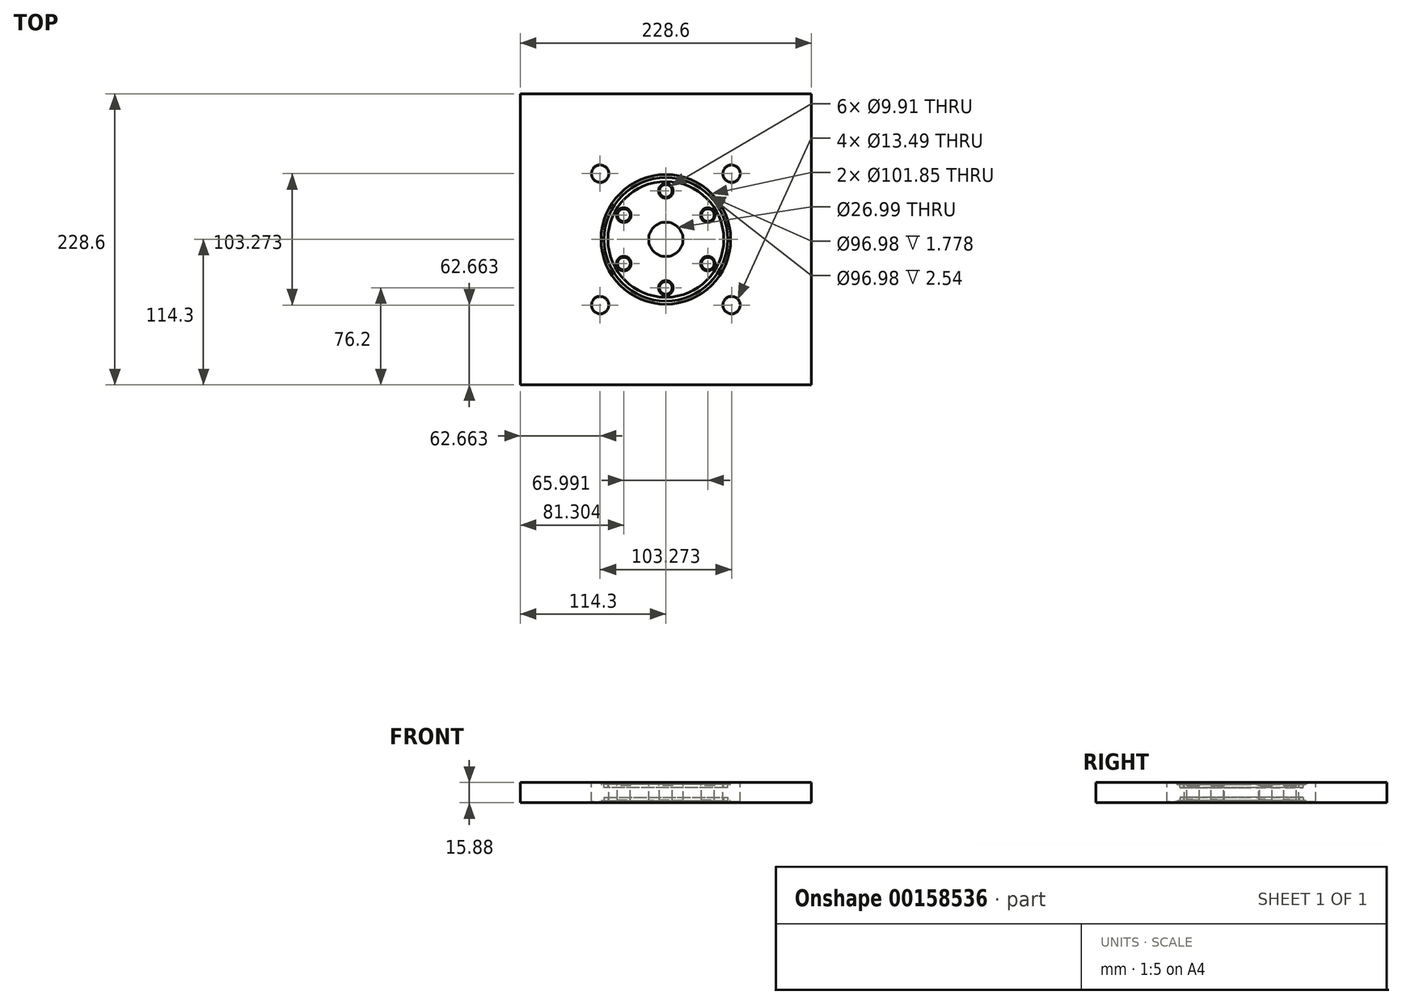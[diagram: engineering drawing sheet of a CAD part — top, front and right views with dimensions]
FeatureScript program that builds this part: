
annotation { "Feature Type Name" : "Feature", "Feature Type Description" : "" }
export const myFeature = defineFeature(function(context is Context, id is Id, definition is map)
    precondition{}
    {
        {
            var Q0;
            Q0=qCreatedBy(makeId("Top.planeOp"),FACE);
            var sketch = newSketch(context, id + "F0", { "sketchPlane" : qUnion([Q0])});
            skCircle(sketch, "E0", {"center": v(0, 0) * mm, "radius": 95.25 * mm});
            skLineSegment(sketch, "E1", {"start": v(-114.3, 114.3) * mm, "end": v(-98.43, 114.3) * mm});
            skLineSegment(sketch, "E2", {"start": v(-114.3, 114.3) * mm, "end": v(-114.3, 74.18) * mm});
            skLineSegment(sketch, "E3", {"start": v(-114.3, 74.18) * mm, "end": v(-89.8, 31.75) * mm});
            skLineSegment(sketch, "E4", {"start": v(-98.43, 114.3) * mm, "end": v(-58.95, 74.82) * mm});
            skLineSegment(sketch, "E5", {"start": v(0, 150.47) * mm, "end": v(0, -152.8) * mm, "construction": true});
            skLineSegment(sketch, "E6.MirrorCS", {"start": v(114.3, 74.18) * mm, "end": v(89.8, 31.75) * mm});
            skLineSegment(sketch, "E7.MirrorCS", {"start": v(114.3, 114.3) * mm, "end": v(114.3, 74.18) * mm});
            skLineSegment(sketch, "E8.MirrorCS", {"start": v(98.42, 114.3) * mm, "end": v(58.95, 74.82) * mm});
            skLineSegment(sketch, "E9.MirrorCS", {"start": v(114.3, 114.3) * mm, "end": v(98.43, 114.3) * mm});
            skLineSegment(sketch, "E10", {"start": v(-127.05, 0) * mm, "end": v(124.38, 0) * mm, "construction": true});
            skLineSegment(sketch, "E11.MirrorCS", {"start": v(-114.3, -114.3) * mm, "end": v(-98.43, -114.3) * mm});
            skLineSegment(sketch, "E12.MirrorCS", {"start": v(114.3, -114.3) * mm, "end": v(98.43, -114.3) * mm});
            skLineSegment(sketch, "E13.MirrorCS", {"start": v(-114.3, -74.18) * mm, "end": v(-89.8, -31.75) * mm});
            skLineSegment(sketch, "E14.MirrorCS", {"start": v(-98.42, -114.3) * mm, "end": v(-58.95, -74.82) * mm});
            skLineSegment(sketch, "E15.MirrorCS", {"start": v(-114.3, -114.3) * mm, "end": v(-114.3, -74.18) * mm});
            skLineSegment(sketch, "E16.MirrorCS", {"start": v(98.43, -114.3) * mm, "end": v(58.95, -74.82) * mm});
            skLineSegment(sketch, "E17.MirrorCS", {"start": v(114.3, -114.3) * mm, "end": v(114.3, -74.18) * mm});
            skLineSegment(sketch, "E18.MirrorCS", {"start": v(114.3, -74.18) * mm, "end": v(89.8, -31.75) * mm});
            skLineSegment(sketch, "E19", {"start": v(-98.43, 114.3) * mm, "end": v(98.43, 114.3) * mm});
            skLineSegment(sketch, "E20", {"start": v(114.3, 74.18) * mm, "end": v(114.3, -74.18) * mm});
            skLineSegment(sketch, "E21", {"start": v(98.43, -114.3) * mm, "end": v(-98.43, -114.3) * mm});
            skLineSegment(sketch, "E22", {"start": v(-114.3, -74.18) * mm, "end": v(-114.3, 74.18) * mm});
            skSolve(sketch);
        }
        {
            var Q0;
            {var subQ1=sQuery(id+"F0.wireOp",EDGE,"E6.MirrorCS");Q0=makeQuery(id+"F0.imprint","IMPRINT",FACE,{"disambiguationData":[TD([[makeQuery(id+"F0.imprint","IMPRINT",EDGE,{"derivedFrom":subQ1}),-1.0]])]});}
            var Q1;
            Q1=makeQuery(id+"F0.imprint","IMPRINT",FACE,{"disambiguationData":[TD([[makeQuery(id+"F0.imprint","IMPRINT",EDGE,{"derivedFrom":sQuery(id+"F0.wireOp",EDGE,"E1")}),-1.0]])]});
            var Q2;
            Q2=makeQuery(id+"F0.imprint","IMPRINT",FACE,{"disambiguationData":[TD([[makeQuery(id+"F0.imprint","IMPRINT",EDGE,{"derivedFrom":sQuery(id+"F0.wireOp",EDGE,"E11.MirrorCS")}),1.0]])]});
            var Q3;
            Q3=makeQuery(id+"F0.imprint","IMPRINT",FACE,{"disambiguationData":[TD([[makeQuery(id+"F0.imprint","IMPRINT",EDGE,{"derivedFrom":sQuery(id+"F0.wireOp",EDGE,"E12.MirrorCS")}),-1.0]])]});
            var Q4;
            {var subQ0=sQuery(id+"F0.wireOp",EDGE,"E0");var subQ5=makeQuery(id+"F0.imprint","INTERSECT",VERTEX,{"derivedFrom":[subQ0,sQuery(id+"F0.wireOp",EDGE,"E6.MirrorCS")]});Q4=makeQuery(id+"F0.imprint","IMPRINT",FACE,{"disambiguationData":[TD([[makeQuery(id+"F0.imprint","IMPRINT",EDGE,{"disambiguationData":[TD([[subQ5,-1.0]])],"derivedFrom":subQ0}),1.0]])]});}
            var Q5;
            Q5 = qSketchRegion(id + "F2", true);
            var Q6;
            {var subQ0=sQuery(id+"F0.wireOp",EDGE,"E4");Q6=makeQuery(id+"F0.imprint","IMPRINT",FACE,{"disambiguationData":[TD([[makeQuery(id+"F0.imprint","IMPRINT",EDGE,{"derivedFrom":subQ0}),1.0]])]});}
            var Q7;
            {var subQ0=sQuery(id+"F0.wireOp",EDGE,"E6.MirrorCS");Q7=makeQuery(id+"F0.imprint","IMPRINT",FACE,{"disambiguationData":[TD([[makeQuery(id+"F0.imprint","IMPRINT",EDGE,{"derivedFrom":subQ0}),1.0]])]});}
            var Q8;
            {var subQ0=sQuery(id+"F0.wireOp",EDGE,"E14.MirrorCS");Q8=makeQuery(id+"F0.imprint","IMPRINT",FACE,{"disambiguationData":[TD([[makeQuery(id+"F0.imprint","IMPRINT",EDGE,{"derivedFrom":subQ0}),-1.0]])]});}
            var Q9;
            {var subQ0=sQuery(id+"F0.wireOp",EDGE,"E3");Q9=makeQuery(id+"F0.imprint","IMPRINT",FACE,{"disambiguationData":[TD([[makeQuery(id+"F0.imprint","IMPRINT",EDGE,{"derivedFrom":subQ0}),-1.0]])]});}
            extrude(context, id + "F1", {"entities" : qUnion([Q0, Q1, Q2, Q3, Q4, Q5, Q6, Q7, Q8, Q9]), "depth" : 15.88 * mm});
        }
        {
            var Q0;
            Q0=makeQuery(id+"F1.opExtrude","CAP_FACE",FACE,{"disambiguationData":[OSD([sQuery(id+"F0.wireOp",EDGE,"E0"),sQuery(id+"F0.wireOp",EDGE,"E1"),sQuery(id+"F0.wireOp",EDGE,"E2"),sQuery(id+"F0.wireOp",EDGE,"E3"),sQuery(id+"F0.wireOp",EDGE,"E4"),sQuery(id+"F0.wireOp",EDGE,"E6.MirrorCS"),sQuery(id+"F0.wireOp",EDGE,"E7.MirrorCS"),sQuery(id+"F0.wireOp",EDGE,"E8.MirrorCS"),sQuery(id+"F0.wireOp",EDGE,"E9.MirrorCS"),sQuery(id+"F0.wireOp",EDGE,"E11.MirrorCS"),sQuery(id+"F0.wireOp",EDGE,"E12.MirrorCS"),sQuery(id+"F0.wireOp",EDGE,"E13.MirrorCS"),sQuery(id+"F0.wireOp",EDGE,"E14.MirrorCS"),sQuery(id+"F0.wireOp",EDGE,"E15.MirrorCS"),sQuery(id+"F0.wireOp",EDGE,"E16.MirrorCS"),sQuery(id+"F0.wireOp",EDGE,"E17.MirrorCS"),sQuery(id+"F0.wireOp",EDGE,"E18.MirrorCS")])],"isStart":false});
            var sketch = newSketch(context, id + "F2", { "sketchPlane" : qUnion([Q0])});
            skLineSegment(sketch, "E23", {"start": v(0, 0) * mm, "end": v(74.38, 0) * mm, "construction": true});
            skLineSegment(sketch, "E24", {"start": v(0, 0) * mm, "end": v(51.64, 51.64) * mm, "construction": true});
            skCircle(sketch, "E25", {"center": v(51.64, 51.64) * mm, "radius": 6.75 * mm});
            skCircle(sketch, "E26.1.0", {"center": v(-51.64, 51.64) * mm, "radius": 6.75 * mm});
            skCircle(sketch, "E26.2.0", {"center": v(-51.64, -51.64) * mm, "radius": 6.75 * mm});
            skCircle(sketch, "E26.3.0", {"center": v(51.64, -51.64) * mm, "radius": 6.75 * mm});
            skPoint(sketch, "E26.center", {"position": v(0, 0) * mm});
            skSolve(sketch);
        }
        {
            var Q0;
            Q0 = qSketchRegion(id + "F2", true);
            extrude(context, id + "F3", {"entities" : qUnion([Q0]), "operationType" : NewBodyOperationType.REMOVE, "oppositeDirection" : true, "depth" : 25.4 * mm});
        }
        {
            var Q0;
            Q0=makeQuery(id+"F1.opExtrude","CAP_FACE",FACE,{"disambiguationData":[OSD([sQuery(id+"F0.wireOp",EDGE,"E1"),sQuery(id+"F0.wireOp",EDGE,"E2"),sQuery(id+"F0.wireOp",EDGE,"E7.MirrorCS"),sQuery(id+"F0.wireOp",EDGE,"E9.MirrorCS"),sQuery(id+"F0.wireOp",EDGE,"E11.MirrorCS"),sQuery(id+"F0.wireOp",EDGE,"E12.MirrorCS"),sQuery(id+"F0.wireOp",EDGE,"E15.MirrorCS"),sQuery(id+"F0.wireOp",EDGE,"E17.MirrorCS"),sQuery(id+"F0.wireOp",EDGE,"E19"),sQuery(id+"F0.wireOp",EDGE,"E20"),sQuery(id+"F0.wireOp",EDGE,"E21"),sQuery(id+"F0.wireOp",EDGE,"E22")])],"isStart":false});
            var sketch = newSketch(context, id + "F4", { "sketchPlane" : qUnion([Q0])});
            skCircle(sketch, "E27", {"center": v(0, 0) * mm, "radius": 50.93 * mm});
            skCircle(sketch, "E28", {"center": v(0, 0) * mm, "radius": 13.5 * mm});
            skSolve(sketch);
        }
        {
            var Q0;
            Q0=makeQuery(id+"F4.imprint","IMPRINT",FACE,{"disambiguationData":[TD([[makeQuery(id+"F4.imprint","IMPRINT",EDGE,{"derivedFrom":sQuery(id+"F4.wireOp",EDGE,"E27")}),1.0]])]});
            extrude(context, id + "F5", {"entities" : qUnion([Q0]), "operationType" : NewBodyOperationType.REMOVE, "oppositeDirection" : true, "depth" : 1.59 * mm});
        }
        {
            var Q0;
            Q0=makeQuery(id+"F4.imprint","IMPRINT",FACE,{"disambiguationData":[TD([[makeQuery(id+"F4.imprint","IMPRINT",EDGE,{"derivedFrom":sQuery(id+"F4.wireOp",EDGE,"E28")}),1.0]])]});
            extrude(context, id + "F6", {"entities" : qUnion([Q0]), "operationType" : NewBodyOperationType.REMOVE, "oppositeDirection" : true, "depth" : 25.4 * mm});
        }
        {
            var Q0;
            Q0=makeQuery(id+"F1.opExtrude","CAP_FACE",FACE,{"disambiguationData":[OSD([sQuery(id+"F0.wireOp",EDGE,"E1"),sQuery(id+"F0.wireOp",EDGE,"E2"),sQuery(id+"F0.wireOp",EDGE,"E7.MirrorCS"),sQuery(id+"F0.wireOp",EDGE,"E9.MirrorCS"),sQuery(id+"F0.wireOp",EDGE,"E11.MirrorCS"),sQuery(id+"F0.wireOp",EDGE,"E12.MirrorCS"),sQuery(id+"F0.wireOp",EDGE,"E15.MirrorCS"),sQuery(id+"F0.wireOp",EDGE,"E17.MirrorCS"),sQuery(id+"F0.wireOp",EDGE,"E19"),sQuery(id+"F0.wireOp",EDGE,"E20"),sQuery(id+"F0.wireOp",EDGE,"E21"),sQuery(id+"F0.wireOp",EDGE,"E22")])],"isStart":true});
            var sketch = newSketch(context, id + "F7", { "sketchPlane" : qUnion([Q0])});
            skCircle(sketch, "E29", {"center": v(0, 0) * mm, "radius": 50.93 * mm});
            skSolve(sketch);
        }
        {
            var Q0;
            Q0=makeQuery(id+"F7.imprint","IMPRINT",FACE,{"disambiguationData":[TD([[makeQuery(id+"F7.imprint","IMPRINT",EDGE,{"derivedFrom":sQuery(id+"F7.wireOp",EDGE,"E29")}),1.0]])]});
            extrude(context, id + "F8", {"entities" : qUnion([Q0]), "operationType" : NewBodyOperationType.REMOVE, "oppositeDirection" : true, "depth" : 1.59 * mm});
        }
        {
            var Q0;
            Q0=makeQuery(id+"F4.imprint","IMPRINT",FACE,{"disambiguationData":[TD([[makeQuery(id+"F4.imprint","IMPRINT",EDGE,{"derivedFrom":sQuery(id+"F4.wireOp",EDGE,"E27")}),1.0]])]});
            var sketch = newSketch(context, id + "F9", { "sketchPlane" : qUnion([Q0])});
            skCircle(sketch, "E30", {"center": v(0, 38.1) * mm, "radius": 4.95 * mm});
            skCircle(sketch, "E31.1.0", {"center": v(-33, 19.05) * mm, "radius": 4.95 * mm});
            skCircle(sketch, "E31.2.0", {"center": v(-33, -19.05) * mm, "radius": 4.95 * mm});
            skCircle(sketch, "E31.3.0", {"center": v(0, -38.1) * mm, "radius": 4.95 * mm});
            skCircle(sketch, "E31.4.0", {"center": v(33, -19.05) * mm, "radius": 4.95 * mm});
            skCircle(sketch, "E31.5.0", {"center": v(33, 19.05) * mm, "radius": 4.95 * mm});
            skPoint(sketch, "E31.center", {"position": v(0, 0) * mm});
            skCircle(sketch, "E32", {"center": v(0, 0) * mm, "radius": 48.49 * mm});
            skCircle(sketch, "E33", {"center": v(0, 0) * mm, "radius": 45.5 * mm});
            skSolve(sketch);
        }
        {
            var Q0;
            Q0=makeQuery(id+"F9.imprint","IMPRINT",FACE,{"disambiguationData":[TD([[makeQuery(id+"F9.imprint","IMPRINT",EDGE,{"derivedFrom":sQuery(id+"F9.wireOp",EDGE,"E30")}),1.0]])]});
            var Q1;
            Q1=makeQuery(id+"F9.imprint","IMPRINT",FACE,{"disambiguationData":[TD([[makeQuery(id+"F9.imprint","IMPRINT",EDGE,{"derivedFrom":sQuery(id+"F9.wireOp",EDGE,"E31.5.0")}),1.0]])]});
            var Q2;
            Q2=makeQuery(id+"F9.imprint","IMPRINT",FACE,{"disambiguationData":[TD([[makeQuery(id+"F9.imprint","IMPRINT",EDGE,{"derivedFrom":sQuery(id+"F9.wireOp",EDGE,"E31.1.0")}),1.0]])]});
            var Q3;
            Q3=makeQuery(id+"F9.imprint","IMPRINT",FACE,{"disambiguationData":[TD([[makeQuery(id+"F9.imprint","IMPRINT",EDGE,{"derivedFrom":sQuery(id+"F9.wireOp",EDGE,"E31.2.0")}),1.0]])]});
            var Q4;
            Q4=makeQuery(id+"F9.imprint","IMPRINT",FACE,{"disambiguationData":[TD([[makeQuery(id+"F9.imprint","IMPRINT",EDGE,{"derivedFrom":sQuery(id+"F9.wireOp",EDGE,"E31.3.0")}),1.0]])]});
            var Q5;
            Q5=makeQuery(id+"F9.imprint","IMPRINT",FACE,{"disambiguationData":[TD([[makeQuery(id+"F9.imprint","IMPRINT",EDGE,{"derivedFrom":sQuery(id+"F9.wireOp",EDGE,"E31.4.0")}),1.0]])]});
            extrude(context, id + "F10", {"entities" : qUnion([Q0, Q1, Q2, Q3, Q4, Q5]), "operationType" : NewBodyOperationType.REMOVE, "oppositeDirection" : true, "depth" : 25.4 * mm});
        }
        {
            var Q0;
            Q0=makeQuery(id+"F9.imprint","IMPRINT",FACE,{"disambiguationData":[TD([[makeQuery(id+"F9.imprint","IMPRINT",EDGE,{"derivedFrom":sQuery(id+"F9.wireOp",EDGE,"E32")}),1.0]])]});
            extrude(context, id + "F11", {"entities" : qUnion([Q0]), "operationType" : NewBodyOperationType.REMOVE, "oppositeDirection" : true, "depth" : 4.13 * mm});
        }
        {
            var Q0;
            Q0=makeQuery(id+"F8.boolean.opBoolean","COPY",FACE,{"derivedFrom":makeQuery(id+"F8.opExtrude","CAP_FACE",FACE,{"disambiguationData":[OSD([sQuery(id+"F0.wireOp",EDGE,"E1"),sQuery(id+"F0.wireOp",EDGE,"E2"),sQuery(id+"F0.wireOp",EDGE,"E7.MirrorCS"),sQuery(id+"F0.wireOp",EDGE,"E9.MirrorCS"),sQuery(id+"F0.wireOp",EDGE,"E11.MirrorCS"),sQuery(id+"F0.wireOp",EDGE,"E12.MirrorCS"),sQuery(id+"F0.wireOp",EDGE,"E15.MirrorCS"),sQuery(id+"F0.wireOp",EDGE,"E17.MirrorCS"),sQuery(id+"F0.wireOp",EDGE,"E19"),sQuery(id+"F0.wireOp",EDGE,"E20"),sQuery(id+"F0.wireOp",EDGE,"E21"),sQuery(id+"F0.wireOp",EDGE,"E22"),sQuery(id+"F4.wireOp",EDGE,"E28"),sQuery(id+"F7.wireOp",EDGE,"E29")])],"isStart":false})});
            var sketch = newSketch(context, id + "F12", { "sketchPlane" : qUnion([Q0])});
            skCircle(sketch, "E34", {"center": v(0, 0) * mm, "radius": 48.49 * mm});
            skCircle(sketch, "E35", {"center": v(0, 0) * mm, "radius": 45.5 * mm});
            skSolve(sketch);
        }
        {
            var Q0;
            Q0=makeQuery(id+"F12.imprint","IMPRINT",FACE,{"disambiguationData":[TD([[makeQuery(id+"F12.imprint","IMPRINT",EDGE,{"derivedFrom":sQuery(id+"F12.wireOp",EDGE,"E34")}),1.0]])]});
            extrude(context, id + "F13", {"entities" : qUnion([Q0]), "operationType" : NewBodyOperationType.REMOVE, "oppositeDirection" : true, "depth" : 2.54 * mm});
        }
        {
            var Q0;
            Q0=makeQuery(id+"F8.boolean.opBoolean","COPY",EDGE,{"derivedFrom":makeQuery(id+"F8.opExtrude","CAP_EDGE",EDGE,{"disambiguationData":[OSD([sQuery(id+"F7.wireOp",EDGE,"E29")])],"isStart":true})});
            var Q1;
            Q1=makeQuery(id+"F8.boolean.opBoolean","COPY",EDGE,{"derivedFrom":makeQuery(id+"F8.opExtrude","CAP_EDGE",EDGE,{"disambiguationData":[OSD([sQuery(id+"F7.wireOp",EDGE,"E29")])],"isStart":false})});
            var Q2;
            Q2=makeQuery(id+"F13.boolean.opBoolean","COPY",EDGE,{"derivedFrom":makeQuery(id+"F13.opExtrude","CAP_EDGE",EDGE,{"disambiguationData":[OSD([sQuery(id+"F12.wireOp",EDGE,"E34")])],"isStart":true})});
            var Q3;
            Q3=makeQuery(id+"F13.boolean.opBoolean","COPY",EDGE,{"derivedFrom":makeQuery(id+"F13.opExtrude","CAP_EDGE",EDGE,{"disambiguationData":[OSD([sQuery(id+"F12.wireOp",EDGE,"E35")])],"isStart":true})});
            var Q4;
            Q4=makeQuery(id+"F8.boolean.opBoolean","COPY",EDGE,{"derivedFrom":makeQuery(id+"F8.opExtrude","CAP_EDGE",EDGE,{"disambiguationData":[OSD([sQuery(id+"F0.wireOp",EDGE,"E1"),sQuery(id+"F0.wireOp",EDGE,"E2"),sQuery(id+"F0.wireOp",EDGE,"E7.MirrorCS"),sQuery(id+"F0.wireOp",EDGE,"E9.MirrorCS"),sQuery(id+"F0.wireOp",EDGE,"E11.MirrorCS"),sQuery(id+"F0.wireOp",EDGE,"E12.MirrorCS"),sQuery(id+"F0.wireOp",EDGE,"E15.MirrorCS"),sQuery(id+"F0.wireOp",EDGE,"E17.MirrorCS"),sQuery(id+"F0.wireOp",EDGE,"E19"),sQuery(id+"F0.wireOp",EDGE,"E20"),sQuery(id+"F0.wireOp",EDGE,"E21"),sQuery(id+"F0.wireOp",EDGE,"E22"),sQuery(id+"F4.wireOp",EDGE,"E28")])],"isStart":false})});
            var Q5;
            Q5=makeQuery(id+"F5.boolean.opBoolean","COPY",EDGE,{"derivedFrom":makeQuery(id+"F5.opExtrude","CAP_EDGE",EDGE,{"disambiguationData":[OSD([sQuery(id+"F4.wireOp",EDGE,"E28")])],"isStart":false})});
            var Q6;
            Q6=makeQuery(id+"F11.boolean.opBoolean","INTERSECT",EDGE,{"derivedFrom":[makeQuery(id+"F5.boolean.opBoolean","COPY",FACE,{"derivedFrom":makeQuery(id+"F5.opExtrude","CAP_FACE",FACE,{"disambiguationData":[OSD([sQuery(id+"F4.wireOp",EDGE,"E27"),sQuery(id+"F4.wireOp",EDGE,"E28")])],"isStart":false})}),makeQuery(id+"F11.opExtrude","SWEPT_FACE",FACE,{"disambiguationData":[OSD([sQuery(id+"F9.wireOp",EDGE,"E32")])]})]});
            var Q7;
            Q7=makeQuery(id+"F5.boolean.opBoolean","COPY",EDGE,{"derivedFrom":makeQuery(id+"F5.opExtrude","CAP_EDGE",EDGE,{"disambiguationData":[OSD([sQuery(id+"F4.wireOp",EDGE,"E27")])],"isStart":false})});
            var Q8;
            Q8=makeQuery(id+"F5.boolean.opBoolean","COPY",EDGE,{"derivedFrom":makeQuery(id+"F5.opExtrude","CAP_EDGE",EDGE,{"disambiguationData":[OSD([sQuery(id+"F4.wireOp",EDGE,"E27")])],"isStart":true})});
            var Q9;
            Q9=makeQuery(id+"F11.boolean.opBoolean","INTERSECT",EDGE,{"derivedFrom":[makeQuery(id+"F5.boolean.opBoolean","COPY",FACE,{"derivedFrom":makeQuery(id+"F5.opExtrude","CAP_FACE",FACE,{"disambiguationData":[OSD([sQuery(id+"F4.wireOp",EDGE,"E27"),sQuery(id+"F4.wireOp",EDGE,"E28")])],"isStart":false})}),makeQuery(id+"F11.opExtrude","SWEPT_FACE",FACE,{"disambiguationData":[OSD([sQuery(id+"F9.wireOp",EDGE,"E33")])]})]});
            fillet(context, id + "F14", {"entities" : qUnion([Q0, Q1, Q2, Q3, Q4, Q5, Q6, Q7, Q8, Q9]), "radius" : 0.76 * mm, "tangentPropagation" : true, "allowEdgeOverflow" : false});
        }
        {
            var Q0;
            Q0=makeQuery(id+"F3.boolean.opBoolean","COPY",EDGE,{"derivedFrom":makeQuery(id+"F3.opExtrude","CAP_EDGE",EDGE,{"disambiguationData":[OSD([sQuery(id+"F2.wireOp",EDGE,"E25")])],"isStart":true})});
            var Q1;
            Q1=makeQuery(id+"F3.boolean.opBoolean","INTERSECT",EDGE,{"derivedFrom":[makeQuery(id+"F1.opExtrude","CAP_FACE",FACE,{"disambiguationData":[OSD([sQuery(id+"F0.wireOp",EDGE,"E1"),sQuery(id+"F0.wireOp",EDGE,"E2"),sQuery(id+"F0.wireOp",EDGE,"E7.MirrorCS"),sQuery(id+"F0.wireOp",EDGE,"E9.MirrorCS"),sQuery(id+"F0.wireOp",EDGE,"E11.MirrorCS"),sQuery(id+"F0.wireOp",EDGE,"E12.MirrorCS"),sQuery(id+"F0.wireOp",EDGE,"E15.MirrorCS"),sQuery(id+"F0.wireOp",EDGE,"E17.MirrorCS"),sQuery(id+"F0.wireOp",EDGE,"E19"),sQuery(id+"F0.wireOp",EDGE,"E20"),sQuery(id+"F0.wireOp",EDGE,"E21"),sQuery(id+"F0.wireOp",EDGE,"E22")])],"isStart":true}),makeQuery(id+"F3.opExtrude","SWEPT_FACE",FACE,{"disambiguationData":[OSD([sQuery(id+"F2.wireOp",EDGE,"E25")])]})]});
            var Q2;
            Q2=makeQuery(id+"F3.boolean.opBoolean","COPY",EDGE,{"derivedFrom":makeQuery(id+"F3.opExtrude","CAP_EDGE",EDGE,{"disambiguationData":[OSD([sQuery(id+"F2.wireOp",EDGE,"E26.3.0")])],"isStart":true})});
            var Q3;
            Q3=makeQuery(id+"F3.boolean.opBoolean","INTERSECT",EDGE,{"derivedFrom":[makeQuery(id+"F1.opExtrude","CAP_FACE",FACE,{"disambiguationData":[OSD([sQuery(id+"F0.wireOp",EDGE,"E1"),sQuery(id+"F0.wireOp",EDGE,"E2"),sQuery(id+"F0.wireOp",EDGE,"E7.MirrorCS"),sQuery(id+"F0.wireOp",EDGE,"E9.MirrorCS"),sQuery(id+"F0.wireOp",EDGE,"E11.MirrorCS"),sQuery(id+"F0.wireOp",EDGE,"E12.MirrorCS"),sQuery(id+"F0.wireOp",EDGE,"E15.MirrorCS"),sQuery(id+"F0.wireOp",EDGE,"E17.MirrorCS"),sQuery(id+"F0.wireOp",EDGE,"E19"),sQuery(id+"F0.wireOp",EDGE,"E20"),sQuery(id+"F0.wireOp",EDGE,"E21"),sQuery(id+"F0.wireOp",EDGE,"E22")])],"isStart":true}),makeQuery(id+"F3.opExtrude","SWEPT_FACE",FACE,{"disambiguationData":[OSD([sQuery(id+"F2.wireOp",EDGE,"E26.3.0")])]})]});
            var Q4;
            Q4=makeQuery(id+"F3.boolean.opBoolean","INTERSECT",EDGE,{"derivedFrom":[makeQuery(id+"F1.opExtrude","CAP_FACE",FACE,{"disambiguationData":[OSD([sQuery(id+"F0.wireOp",EDGE,"E1"),sQuery(id+"F0.wireOp",EDGE,"E2"),sQuery(id+"F0.wireOp",EDGE,"E7.MirrorCS"),sQuery(id+"F0.wireOp",EDGE,"E9.MirrorCS"),sQuery(id+"F0.wireOp",EDGE,"E11.MirrorCS"),sQuery(id+"F0.wireOp",EDGE,"E12.MirrorCS"),sQuery(id+"F0.wireOp",EDGE,"E15.MirrorCS"),sQuery(id+"F0.wireOp",EDGE,"E17.MirrorCS"),sQuery(id+"F0.wireOp",EDGE,"E19"),sQuery(id+"F0.wireOp",EDGE,"E20"),sQuery(id+"F0.wireOp",EDGE,"E21"),sQuery(id+"F0.wireOp",EDGE,"E22")])],"isStart":true}),makeQuery(id+"F3.opExtrude","SWEPT_FACE",FACE,{"disambiguationData":[OSD([sQuery(id+"F2.wireOp",EDGE,"E26.1.0")])]})]});
            var Q5;
            Q5=makeQuery(id+"F3.boolean.opBoolean","COPY",EDGE,{"derivedFrom":makeQuery(id+"F3.opExtrude","CAP_EDGE",EDGE,{"disambiguationData":[OSD([sQuery(id+"F2.wireOp",EDGE,"E26.1.0")])],"isStart":true})});
            var Q6;
            Q6=makeQuery(id+"F3.boolean.opBoolean","INTERSECT",EDGE,{"derivedFrom":[makeQuery(id+"F1.opExtrude","CAP_FACE",FACE,{"disambiguationData":[OSD([sQuery(id+"F0.wireOp",EDGE,"E1"),sQuery(id+"F0.wireOp",EDGE,"E2"),sQuery(id+"F0.wireOp",EDGE,"E7.MirrorCS"),sQuery(id+"F0.wireOp",EDGE,"E9.MirrorCS"),sQuery(id+"F0.wireOp",EDGE,"E11.MirrorCS"),sQuery(id+"F0.wireOp",EDGE,"E12.MirrorCS"),sQuery(id+"F0.wireOp",EDGE,"E15.MirrorCS"),sQuery(id+"F0.wireOp",EDGE,"E17.MirrorCS"),sQuery(id+"F0.wireOp",EDGE,"E19"),sQuery(id+"F0.wireOp",EDGE,"E20"),sQuery(id+"F0.wireOp",EDGE,"E21"),sQuery(id+"F0.wireOp",EDGE,"E22")])],"isStart":true}),makeQuery(id+"F3.opExtrude","SWEPT_FACE",FACE,{"disambiguationData":[OSD([sQuery(id+"F2.wireOp",EDGE,"E26.2.0")])]})]});
            var Q7;
            Q7=makeQuery(id+"F3.boolean.opBoolean","COPY",EDGE,{"derivedFrom":makeQuery(id+"F3.opExtrude","CAP_EDGE",EDGE,{"disambiguationData":[OSD([sQuery(id+"F2.wireOp",EDGE,"E26.2.0")])],"isStart":true})});
            var Q8;
            Q8=makeQuery(id+"F10.boolean.opBoolean","INTERSECT",EDGE,{"derivedFrom":[makeQuery(id+"F8.boolean.opBoolean","COPY",FACE,{"derivedFrom":makeQuery(id+"F8.opExtrude","CAP_FACE",FACE,{"disambiguationData":[OSD([sQuery(id+"F0.wireOp",EDGE,"E1"),sQuery(id+"F0.wireOp",EDGE,"E2"),sQuery(id+"F0.wireOp",EDGE,"E7.MirrorCS"),sQuery(id+"F0.wireOp",EDGE,"E9.MirrorCS"),sQuery(id+"F0.wireOp",EDGE,"E11.MirrorCS"),sQuery(id+"F0.wireOp",EDGE,"E12.MirrorCS"),sQuery(id+"F0.wireOp",EDGE,"E15.MirrorCS"),sQuery(id+"F0.wireOp",EDGE,"E17.MirrorCS"),sQuery(id+"F0.wireOp",EDGE,"E19"),sQuery(id+"F0.wireOp",EDGE,"E20"),sQuery(id+"F0.wireOp",EDGE,"E21"),sQuery(id+"F0.wireOp",EDGE,"E22"),sQuery(id+"F4.wireOp",EDGE,"E28"),sQuery(id+"F7.wireOp",EDGE,"E29")])],"isStart":false})}),makeQuery(id+"F10.opExtrude","SWEPT_FACE",FACE,{"disambiguationData":[OSD([sQuery(id+"F9.wireOp",EDGE,"E30")])]})]});
            var Q9;
            Q9=makeQuery(id+"F10.boolean.opBoolean","INTERSECT",EDGE,{"derivedFrom":[makeQuery(id+"F5.boolean.opBoolean","COPY",FACE,{"derivedFrom":makeQuery(id+"F5.opExtrude","CAP_FACE",FACE,{"disambiguationData":[OSD([sQuery(id+"F4.wireOp",EDGE,"E27"),sQuery(id+"F4.wireOp",EDGE,"E28")])],"isStart":false})}),makeQuery(id+"F10.opExtrude","SWEPT_FACE",FACE,{"disambiguationData":[OSD([sQuery(id+"F9.wireOp",EDGE,"E30")])]})]});
            var Q10;
            Q10=makeQuery(id+"F10.boolean.opBoolean","INTERSECT",EDGE,{"derivedFrom":[makeQuery(id+"F8.boolean.opBoolean","COPY",FACE,{"derivedFrom":makeQuery(id+"F8.opExtrude","CAP_FACE",FACE,{"disambiguationData":[OSD([sQuery(id+"F0.wireOp",EDGE,"E1"),sQuery(id+"F0.wireOp",EDGE,"E2"),sQuery(id+"F0.wireOp",EDGE,"E7.MirrorCS"),sQuery(id+"F0.wireOp",EDGE,"E9.MirrorCS"),sQuery(id+"F0.wireOp",EDGE,"E11.MirrorCS"),sQuery(id+"F0.wireOp",EDGE,"E12.MirrorCS"),sQuery(id+"F0.wireOp",EDGE,"E15.MirrorCS"),sQuery(id+"F0.wireOp",EDGE,"E17.MirrorCS"),sQuery(id+"F0.wireOp",EDGE,"E19"),sQuery(id+"F0.wireOp",EDGE,"E20"),sQuery(id+"F0.wireOp",EDGE,"E21"),sQuery(id+"F0.wireOp",EDGE,"E22"),sQuery(id+"F4.wireOp",EDGE,"E28"),sQuery(id+"F7.wireOp",EDGE,"E29")])],"isStart":false})}),makeQuery(id+"F10.opExtrude","SWEPT_FACE",FACE,{"disambiguationData":[OSD([sQuery(id+"F9.wireOp",EDGE,"E31.5.0")])]})]});
            var Q11;
            Q11=makeQuery(id+"F10.boolean.opBoolean","INTERSECT",EDGE,{"derivedFrom":[makeQuery(id+"F5.boolean.opBoolean","COPY",FACE,{"derivedFrom":makeQuery(id+"F5.opExtrude","CAP_FACE",FACE,{"disambiguationData":[OSD([sQuery(id+"F4.wireOp",EDGE,"E27"),sQuery(id+"F4.wireOp",EDGE,"E28")])],"isStart":false})}),makeQuery(id+"F10.opExtrude","SWEPT_FACE",FACE,{"disambiguationData":[OSD([sQuery(id+"F9.wireOp",EDGE,"E31.5.0")])]})]});
            var Q12;
            Q12=makeQuery(id+"F10.boolean.opBoolean","INTERSECT",EDGE,{"derivedFrom":[makeQuery(id+"F8.boolean.opBoolean","COPY",FACE,{"derivedFrom":makeQuery(id+"F8.opExtrude","CAP_FACE",FACE,{"disambiguationData":[OSD([sQuery(id+"F0.wireOp",EDGE,"E1"),sQuery(id+"F0.wireOp",EDGE,"E2"),sQuery(id+"F0.wireOp",EDGE,"E7.MirrorCS"),sQuery(id+"F0.wireOp",EDGE,"E9.MirrorCS"),sQuery(id+"F0.wireOp",EDGE,"E11.MirrorCS"),sQuery(id+"F0.wireOp",EDGE,"E12.MirrorCS"),sQuery(id+"F0.wireOp",EDGE,"E15.MirrorCS"),sQuery(id+"F0.wireOp",EDGE,"E17.MirrorCS"),sQuery(id+"F0.wireOp",EDGE,"E19"),sQuery(id+"F0.wireOp",EDGE,"E20"),sQuery(id+"F0.wireOp",EDGE,"E21"),sQuery(id+"F0.wireOp",EDGE,"E22"),sQuery(id+"F4.wireOp",EDGE,"E28"),sQuery(id+"F7.wireOp",EDGE,"E29")])],"isStart":false})}),makeQuery(id+"F10.opExtrude","SWEPT_FACE",FACE,{"disambiguationData":[OSD([sQuery(id+"F9.wireOp",EDGE,"E31.4.0")])]})]});
            var Q13;
            Q13=makeQuery(id+"F10.boolean.opBoolean","INTERSECT",EDGE,{"derivedFrom":[makeQuery(id+"F5.boolean.opBoolean","COPY",FACE,{"derivedFrom":makeQuery(id+"F5.opExtrude","CAP_FACE",FACE,{"disambiguationData":[OSD([sQuery(id+"F4.wireOp",EDGE,"E27"),sQuery(id+"F4.wireOp",EDGE,"E28")])],"isStart":false})}),makeQuery(id+"F10.opExtrude","SWEPT_FACE",FACE,{"disambiguationData":[OSD([sQuery(id+"F9.wireOp",EDGE,"E31.4.0")])]})]});
            var Q14;
            Q14=makeQuery(id+"F10.boolean.opBoolean","INTERSECT",EDGE,{"derivedFrom":[makeQuery(id+"F8.boolean.opBoolean","COPY",FACE,{"derivedFrom":makeQuery(id+"F8.opExtrude","CAP_FACE",FACE,{"disambiguationData":[OSD([sQuery(id+"F0.wireOp",EDGE,"E1"),sQuery(id+"F0.wireOp",EDGE,"E2"),sQuery(id+"F0.wireOp",EDGE,"E7.MirrorCS"),sQuery(id+"F0.wireOp",EDGE,"E9.MirrorCS"),sQuery(id+"F0.wireOp",EDGE,"E11.MirrorCS"),sQuery(id+"F0.wireOp",EDGE,"E12.MirrorCS"),sQuery(id+"F0.wireOp",EDGE,"E15.MirrorCS"),sQuery(id+"F0.wireOp",EDGE,"E17.MirrorCS"),sQuery(id+"F0.wireOp",EDGE,"E19"),sQuery(id+"F0.wireOp",EDGE,"E20"),sQuery(id+"F0.wireOp",EDGE,"E21"),sQuery(id+"F0.wireOp",EDGE,"E22"),sQuery(id+"F4.wireOp",EDGE,"E28"),sQuery(id+"F7.wireOp",EDGE,"E29")])],"isStart":false})}),makeQuery(id+"F10.opExtrude","SWEPT_FACE",FACE,{"disambiguationData":[OSD([sQuery(id+"F9.wireOp",EDGE,"E31.3.0")])]})]});
            var Q15;
            Q15=makeQuery(id+"F10.boolean.opBoolean","INTERSECT",EDGE,{"derivedFrom":[makeQuery(id+"F5.boolean.opBoolean","COPY",FACE,{"derivedFrom":makeQuery(id+"F5.opExtrude","CAP_FACE",FACE,{"disambiguationData":[OSD([sQuery(id+"F4.wireOp",EDGE,"E27"),sQuery(id+"F4.wireOp",EDGE,"E28")])],"isStart":false})}),makeQuery(id+"F10.opExtrude","SWEPT_FACE",FACE,{"disambiguationData":[OSD([sQuery(id+"F9.wireOp",EDGE,"E31.3.0")])]})]});
            var Q16;
            Q16=makeQuery(id+"F10.boolean.opBoolean","INTERSECT",EDGE,{"derivedFrom":[makeQuery(id+"F8.boolean.opBoolean","COPY",FACE,{"derivedFrom":makeQuery(id+"F8.opExtrude","CAP_FACE",FACE,{"disambiguationData":[OSD([sQuery(id+"F0.wireOp",EDGE,"E1"),sQuery(id+"F0.wireOp",EDGE,"E2"),sQuery(id+"F0.wireOp",EDGE,"E7.MirrorCS"),sQuery(id+"F0.wireOp",EDGE,"E9.MirrorCS"),sQuery(id+"F0.wireOp",EDGE,"E11.MirrorCS"),sQuery(id+"F0.wireOp",EDGE,"E12.MirrorCS"),sQuery(id+"F0.wireOp",EDGE,"E15.MirrorCS"),sQuery(id+"F0.wireOp",EDGE,"E17.MirrorCS"),sQuery(id+"F0.wireOp",EDGE,"E19"),sQuery(id+"F0.wireOp",EDGE,"E20"),sQuery(id+"F0.wireOp",EDGE,"E21"),sQuery(id+"F0.wireOp",EDGE,"E22"),sQuery(id+"F4.wireOp",EDGE,"E28"),sQuery(id+"F7.wireOp",EDGE,"E29")])],"isStart":false})}),makeQuery(id+"F10.opExtrude","SWEPT_FACE",FACE,{"disambiguationData":[OSD([sQuery(id+"F9.wireOp",EDGE,"E31.2.0")])]})]});
            var Q17;
            Q17=makeQuery(id+"F10.boolean.opBoolean","INTERSECT",EDGE,{"derivedFrom":[makeQuery(id+"F5.boolean.opBoolean","COPY",FACE,{"derivedFrom":makeQuery(id+"F5.opExtrude","CAP_FACE",FACE,{"disambiguationData":[OSD([sQuery(id+"F4.wireOp",EDGE,"E27"),sQuery(id+"F4.wireOp",EDGE,"E28")])],"isStart":false})}),makeQuery(id+"F10.opExtrude","SWEPT_FACE",FACE,{"disambiguationData":[OSD([sQuery(id+"F9.wireOp",EDGE,"E31.2.0")])]})]});
            var Q18;
            Q18=makeQuery(id+"F10.boolean.opBoolean","INTERSECT",EDGE,{"derivedFrom":[makeQuery(id+"F5.boolean.opBoolean","COPY",FACE,{"derivedFrom":makeQuery(id+"F5.opExtrude","CAP_FACE",FACE,{"disambiguationData":[OSD([sQuery(id+"F4.wireOp",EDGE,"E27"),sQuery(id+"F4.wireOp",EDGE,"E28")])],"isStart":false})}),makeQuery(id+"F10.opExtrude","SWEPT_FACE",FACE,{"disambiguationData":[OSD([sQuery(id+"F9.wireOp",EDGE,"E31.1.0")])]})]});
            var Q19;
            Q19=makeQuery(id+"F10.boolean.opBoolean","INTERSECT",EDGE,{"derivedFrom":[makeQuery(id+"F8.boolean.opBoolean","COPY",FACE,{"derivedFrom":makeQuery(id+"F8.opExtrude","CAP_FACE",FACE,{"disambiguationData":[OSD([sQuery(id+"F0.wireOp",EDGE,"E1"),sQuery(id+"F0.wireOp",EDGE,"E2"),sQuery(id+"F0.wireOp",EDGE,"E7.MirrorCS"),sQuery(id+"F0.wireOp",EDGE,"E9.MirrorCS"),sQuery(id+"F0.wireOp",EDGE,"E11.MirrorCS"),sQuery(id+"F0.wireOp",EDGE,"E12.MirrorCS"),sQuery(id+"F0.wireOp",EDGE,"E15.MirrorCS"),sQuery(id+"F0.wireOp",EDGE,"E17.MirrorCS"),sQuery(id+"F0.wireOp",EDGE,"E19"),sQuery(id+"F0.wireOp",EDGE,"E20"),sQuery(id+"F0.wireOp",EDGE,"E21"),sQuery(id+"F0.wireOp",EDGE,"E22"),sQuery(id+"F4.wireOp",EDGE,"E28"),sQuery(id+"F7.wireOp",EDGE,"E29")])],"isStart":false})}),makeQuery(id+"F10.opExtrude","SWEPT_FACE",FACE,{"disambiguationData":[OSD([sQuery(id+"F9.wireOp",EDGE,"E31.1.0")])]})]});
            chamfer(context, id + "F15", {"entities" : qUnion([Q0, Q1, Q2, Q3, Q4, Q5, Q6, Q7, Q8, Q9, Q10, Q11, Q12, Q13, Q14, Q15, Q16, Q17, Q18, Q19]), "width" : 0.76 * mm, "tangentPropagation" : true});
        }
    });
